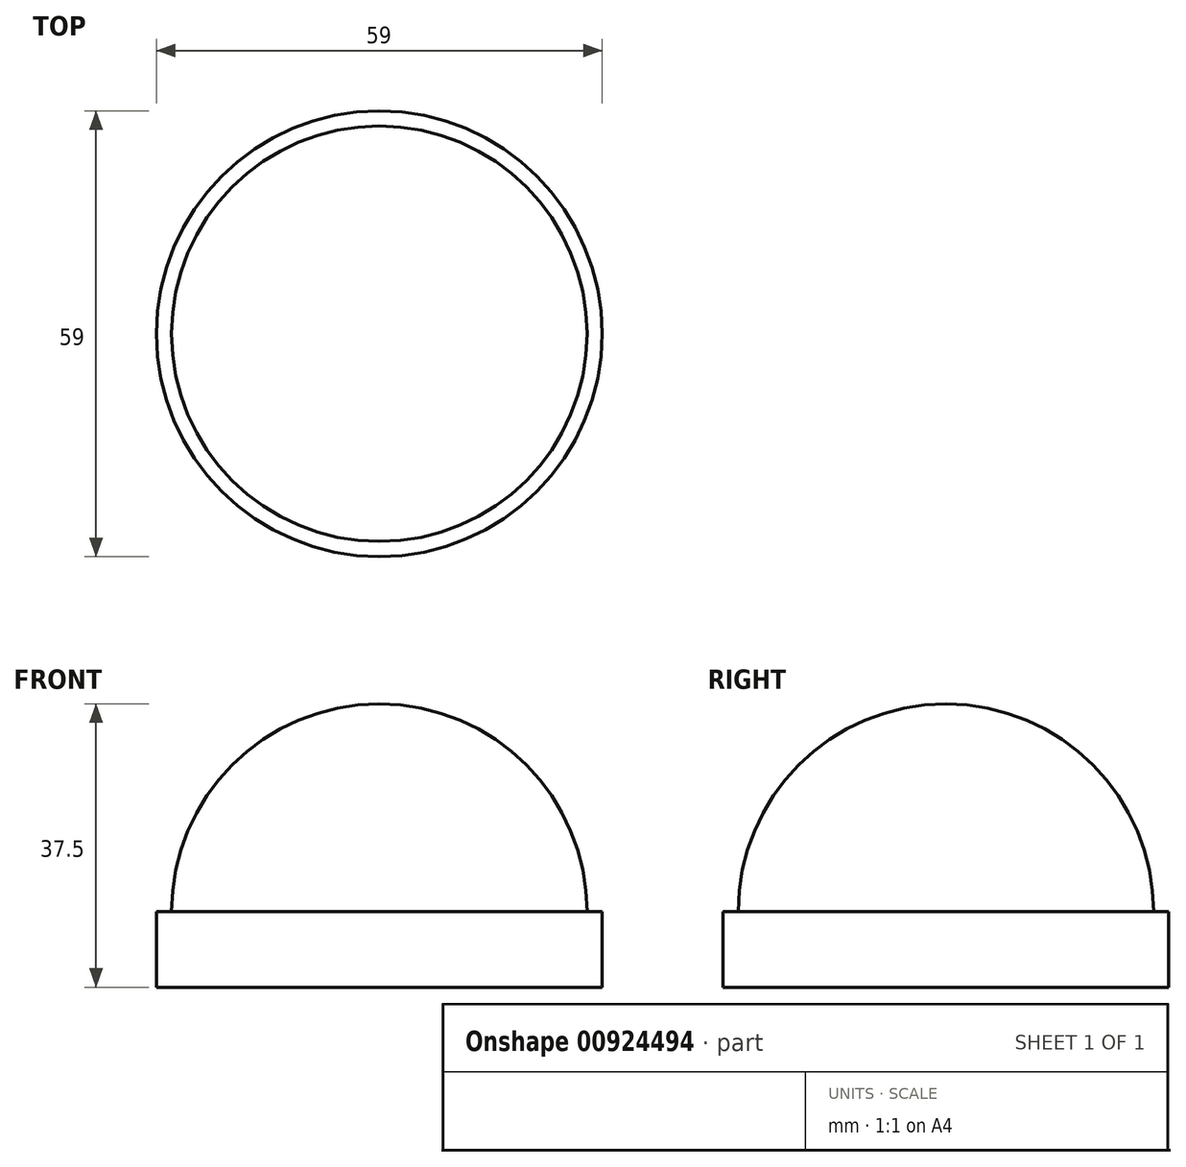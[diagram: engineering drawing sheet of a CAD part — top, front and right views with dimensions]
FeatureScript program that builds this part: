
annotation { "Feature Type Name" : "Feature", "Feature Type Description" : "" }
export const myFeature = defineFeature(function(context is Context, id is Id, definition is map)
    precondition{}
    {
        {
            var Q0;
            Q0=qCreatedBy(makeId("Top.planeOp"),FACE);
            var sketch = newSketch(context, id + "F0", { "sketchPlane" : qUnion([Q0])});
            skCircle(sketch, "E0", {"center": v(0, 0) * mm, "radius": 29.5 * mm});
            skSolve(sketch);
        }
        {
            var Q0;
            Q0=qSketchRegion(id+"F0",true);
            var Q1;
            Q1=makeQuery(id+"F0.imprint","IMPRINT",FACE,{"disambiguationData":[TD([[makeQuery(id+"F0.imprint","IMPRINT",EDGE,{"derivedFrom":sQuery(id+"F0.wireOp",EDGE,"E0")}),1.0]])]});
            extrude(context, id + "F1", {"entities" : qUnion([Q0, Q1]), "depth" : 10 * mm, "offsetDistance" : 25 * mm});
        }
        {
            var Q0;
            Q0=makeQuery(id+"F1.opExtrude","CAP_FACE",FACE,{"disambiguationData":[OSD([sQuery(id+"F0.wireOp",EDGE,"E0")])],"isStart":false});
            var sketch = newSketch(context, id + "F2", { "sketchPlane" : qUnion([Q0])});
            skCircle(sketch, "E1", {"center": v(0, 0) * mm, "radius": 27.5 * mm});
            skLineSegment(sketch, "E2", {"start": v(0, 41.38) * mm, "end": v(0, -45.85) * mm});
            skSolve(sketch);
        }
        {
            var Q0;
            {var subQ0=sQuery(id+"F2.wireOp",EDGE,"E2");var subQ1=sQuery(id+"F2.wireOp",EDGE,"E1");var subQ2=makeQuery(id+"F2.imprint","INTERSECT",VERTEX,{"disambiguationData":[OD(0.0)],"derivedFrom":[subQ1,subQ0]});Q0=makeQuery(id+"F2.imprint","IMPRINT",FACE,{"disambiguationData":[TD([[makeQuery(id+"F2.imprint","IMPRINT",EDGE,{"disambiguationData":[TD([[subQ2,1.0]])],"derivedFrom":subQ1}),1.0]])]});}
            var Q1;
            Q1=sQuery(id+"F2.wireOp",EDGE,"E2");
            revolve(context, id + "F3", {"surfaceOperationType" : NewSurfaceOperationType.NEW, "entities" : qUnion([Q0]), "axis" : qUnion([Q1]), "revolveType" : RevolveType.ONE_DIRECTION, "angle" : 180 * degree});
        }
    });
